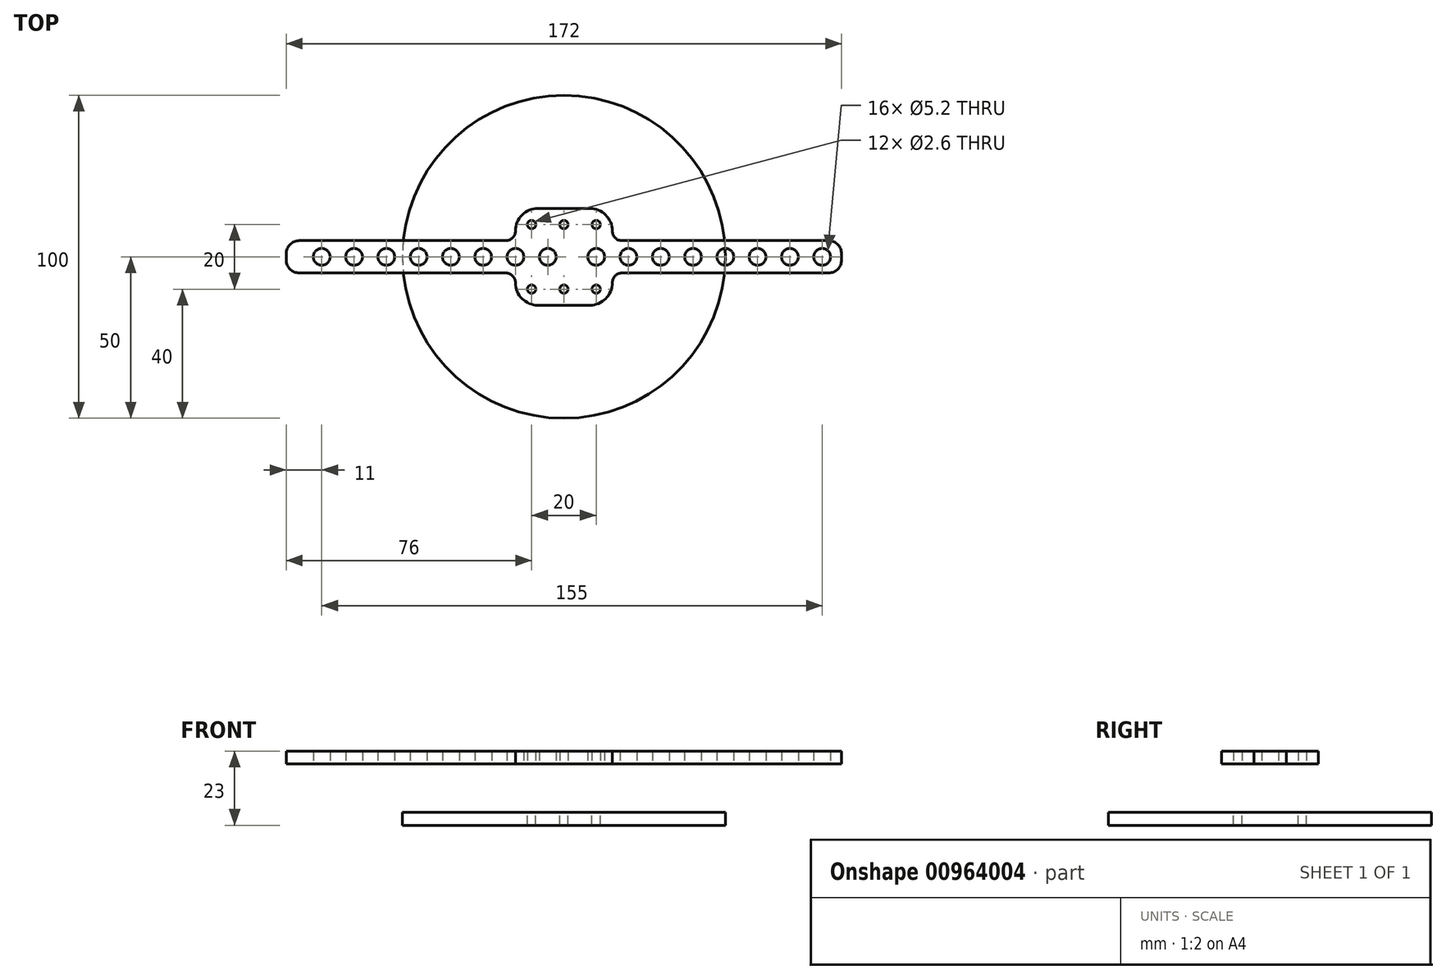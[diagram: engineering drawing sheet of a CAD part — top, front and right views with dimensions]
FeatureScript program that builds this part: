
annotation { "Feature Type Name" : "Feature", "Feature Type Description" : "" }
export const myFeature = defineFeature(function(context is Context, id is Id, definition is map)
    precondition{}
    {
        {
            var Q0;
            Q0=qCreatedBy(makeId("Top.planeOp"),FACE);
            var sketch = newSketch(context, id + "F0", { "sketchPlane" : qUnion([Q0])});
            skLineSegment(sketch, "E0.bottom", {"start": v(-8, 15) * mm, "end": v(8, 15) * mm});
            skLineSegment(sketch, "E0.top", {"start": v(-8, -15) * mm, "end": v(8, -15) * mm});
            skLineSegment(sketch, "E0.left", {"start": v(-15, 8) * mm, "end": v(-15, 8) * mm});
            skLineSegment(sketch, "E0.right", {"start": v(15, 8) * mm, "end": v(15, 8) * mm});
            skPoint(sketch, "E0.middle", {"position": v(0, 0) * mm});
            skLineSegment(sketch, "E1.bottom", {"start": v(-18, 5) * mm, "end": v(-82, 5) * mm});
            skLineSegment(sketch, "E1.top", {"start": v(-18, -5) * mm, "end": v(-82, -5) * mm});
            skLineSegment(sketch, "E1.right", {"start": v(-86, 1) * mm, "end": v(-86, -1) * mm});
            skLineSegment(sketch, "E2.trimOffspring", {"start": v(-15, -8) * mm, "end": v(-15, -8) * mm});
            skLineSegment(sketch, "E3.MirrorCS", {"start": v(86, 1) * mm, "end": v(86, -1) * mm});
            skLineSegment(sketch, "E4.MirrorCS", {"start": v(18, 5) * mm, "end": v(82, 5) * mm});
            skLineSegment(sketch, "E5.MirrorCS", {"start": v(18, -5) * mm, "end": v(82, -5) * mm});
            skPoint(sketch, "E6.visualSharp", {"position": v(-15, 15) * mm});
            skArc(sketch, "E6.filletArc", {"start": v(-8, 15) * mm, "mid": v(-12.95, 12.95) * mm, "end": v(-15, 8) * mm});
            skPoint(sketch, "E7.visualSharp", {"position": v(-15, -15) * mm});
            skArc(sketch, "E7.filletArc", {"start": v(-15, -8) * mm, "mid": v(-12.95, -12.95) * mm, "end": v(-8, -15) * mm});
            skPoint(sketch, "E8.visualSharp", {"position": v(15, -15) * mm});
            skArc(sketch, "E8.filletArc", {"start": v(8, -15) * mm, "mid": v(12.95, -12.95) * mm, "end": v(15, -8) * mm});
            skPoint(sketch, "E9.visualSharp", {"position": v(15, 15) * mm});
            skArc(sketch, "E9.filletArc", {"start": v(15, 8) * mm, "mid": v(12.95, 12.95) * mm, "end": v(8, 15) * mm});
            skPoint(sketch, "E10.visualSharp", {"position": v(-86, 5) * mm});
            skArc(sketch, "E10.filletArc", {"start": v(-82, 5) * mm, "mid": v(-84.83, 3.83) * mm, "end": v(-86, 1) * mm});
            skPoint(sketch, "E11.visualSharp", {"position": v(-86, -5) * mm});
            skArc(sketch, "E11.filletArc", {"start": v(-86, -1) * mm, "mid": v(-84.83, -3.83) * mm, "end": v(-82, -5) * mm});
            skPoint(sketch, "E12.visualSharp", {"position": v(86, 5) * mm});
            skArc(sketch, "E12.filletArc", {"start": v(86, 1) * mm, "mid": v(84.83, 3.83) * mm, "end": v(82, 5) * mm});
            skPoint(sketch, "E13.visualSharp", {"position": v(86, -5) * mm});
            skArc(sketch, "E13.filletArc", {"start": v(82, -5) * mm, "mid": v(84.83, -3.83) * mm, "end": v(86, -1) * mm});
            skPoint(sketch, "E14.visualSharp", {"position": v(-15, -5) * mm});
            skArc(sketch, "E14.filletArc", {"start": v(-15, -8) * mm, "mid": v(-15.88, -5.88) * mm, "end": v(-18, -5) * mm});
            skPoint(sketch, "E15.visualSharp", {"position": v(-15, 5) * mm});
            skArc(sketch, "E15.filletArc", {"start": v(-18, 5) * mm, "mid": v(-15.88, 5.88) * mm, "end": v(-15, 8) * mm});
            skLineSegment(sketch, "E16.trimOffspring", {"start": v(15, -8) * mm, "end": v(15, -8) * mm});
            skPoint(sketch, "E17.visualSharp", {"position": v(15, -5) * mm});
            skArc(sketch, "E17.filletArc", {"start": v(18, -5) * mm, "mid": v(15.88, -5.88) * mm, "end": v(15, -8) * mm});
            skPoint(sketch, "E18.visualSharp", {"position": v(15, 5) * mm});
            skArc(sketch, "E18.filletArc", {"start": v(15, 8) * mm, "mid": v(15.88, 5.88) * mm, "end": v(18, 5) * mm});
            skCircle(sketch, "E19", {"center": v(10, 0) * mm, "radius": 2.6 * mm});
            skCircle(sketch, "E20.1.0.0", {"center": v(20, 0) * mm, "radius": 2.6 * mm});
            skCircle(sketch, "E20.2.0.0", {"center": v(30, 0) * mm, "radius": 2.6 * mm});
            skCircle(sketch, "E20.3.0.0", {"center": v(40, 0) * mm, "radius": 2.6 * mm});
            skCircle(sketch, "E20.4.0.0", {"center": v(50, 0) * mm, "radius": 2.6 * mm});
            skLineSegment(sketch, "E20.direction1", {"start": v(10, 0) * mm, "end": v(20, 0) * mm, "construction": true});
            skCircle(sketch, "E21.0.5.0", {"center": v(60, 0) * mm, "radius": 2.6 * mm});
            skCircle(sketch, "E21.0.6.0", {"center": v(70, 0) * mm, "radius": 2.6 * mm});
            skCircle(sketch, "E21.0.7.0", {"center": v(80, 0) * mm, "radius": 2.6 * mm});
            skCircle(sketch, "E22", {"center": v(-5, 0) * mm, "radius": 2.6 * mm});
            skCircle(sketch, "E23.1.0.0", {"center": v(-15, 0) * mm, "radius": 2.6 * mm});
            skCircle(sketch, "E23.2.0.0", {"center": v(-25, 0) * mm, "radius": 2.6 * mm});
            skCircle(sketch, "E23.3.0.0", {"center": v(-35, 0) * mm, "radius": 2.6 * mm});
            skCircle(sketch, "E23.4.0.0", {"center": v(-45, 0) * mm, "radius": 2.6 * mm});
            skCircle(sketch, "E23.5.0.0", {"center": v(-55, 0) * mm, "radius": 2.6 * mm});
            skCircle(sketch, "E23.6.0.0", {"center": v(-65, 0) * mm, "radius": 2.6 * mm});
            skCircle(sketch, "E23.7.0.0", {"center": v(-75, 0) * mm, "radius": 2.6 * mm});
            skLineSegment(sketch, "E23.direction1", {"start": v(-5, 0) * mm, "end": v(-15, 0) * mm, "construction": true});
            skCircle(sketch, "E24", {"center": v(10, -10) * mm, "radius": 1.3 * mm});
            skCircle(sketch, "E25.0.1.0", {"center": v(10, 10) * mm, "radius": 1.3 * mm});
            skCircle(sketch, "E25.1.0.0", {"center": v(0, -10) * mm, "radius": 1.3 * mm});
            skCircle(sketch, "E25.1.1.0", {"center": v(0, 10) * mm, "radius": 1.3 * mm});
            skCircle(sketch, "E25.2.0.0", {"center": v(-10, -10) * mm, "radius": 1.3 * mm});
            skCircle(sketch, "E25.2.1.0", {"center": v(-10, 10) * mm, "radius": 1.3 * mm});
            skLineSegment(sketch, "E25.direction1", {"start": v(10, -10) * mm, "end": v(0, -10) * mm, "construction": true});
            skLineSegment(sketch, "E25.direction2", {"start": v(10, -10) * mm, "end": v(10, 10) * mm, "construction": true});
            skSolve(sketch);
        }
        {
            var Q0;
            Q0 = qSketchRegion(id + "F0", true);
            extrude(context, id + "F1", {"entities" : qUnion([Q0]), "depth" : 4 * mm, "offsetDistance" : 25 * mm});
        }
        {
            var Q0;
            Q0=qCreatedBy(makeId("Top.planeOp"),FACE);
            cPlane(context, id + "F2", {"entities" : qUnion([Q0]), "cplaneType" : CPlaneType.OFFSET, "offset" : 15 * mm, "oppositeDirection" : true, "width" : 150 * mm, "height" : 150 * mm});
        }
        {
            var Q0;
            Q0=qCreatedBy(id+"F2.planeOp",FACE);
            var sketch = newSketch(context, id + "F3", { "sketchPlane" : qUnion([Q0])});
            skCircle(sketch, "E26.0", {"center": v(-10, -10) * mm, "radius": 1.3 * mm});
            skCircle(sketch, "E27.0", {"center": v(0, -10) * mm, "radius": 1.3 * mm});
            skCircle(sketch, "E28.0", {"center": v(10, -10) * mm, "radius": 1.3 * mm});
            skCircle(sketch, "E29.0", {"center": v(10, 10) * mm, "radius": 1.3 * mm});
            skCircle(sketch, "E30.0", {"center": v(0, 10) * mm, "radius": 1.3 * mm});
            skCircle(sketch, "E31.0", {"center": v(-10, 10) * mm, "radius": 1.3 * mm});
            skCircle(sketch, "E32", {"center": v(0, 0) * mm, "radius": 50 * mm});
            skSolve(sketch);
        }
        {
            var Q0;
            Q0 = qSketchRegion(id + "F3", true);
            extrude(context, id + "F4", {"entities" : qUnion([Q0]), "oppositeDirection" : true, "depth" : 4 * mm, "offsetDistance" : 25 * mm});
        }
    });
